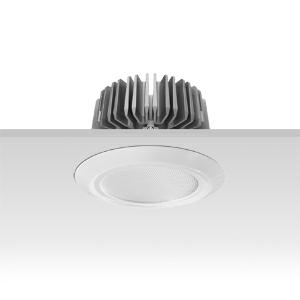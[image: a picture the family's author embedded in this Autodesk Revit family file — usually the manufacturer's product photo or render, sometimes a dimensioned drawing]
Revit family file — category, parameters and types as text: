
# Revit family: 3f_filippi_-_3f_reno_bianco_ampio_3f_filippi_-_30375_a01046_-_3f_reno_150_wh_2000-840_dali_wide___smp_wh_1bde
name_source: partatom
category: Lighting Fixtures
units: mm (PartAtom-declared; Revit-internal decimal feet)

## family parameters
Cut with Voids When Loaded = No
Host = Face
Light Source = No
Part Type = Normal
Room Calculation Point = No
Round Connector Dimension = Use Diameter
Shared = No

## types (1)
- 3F Filippi - 3F Reno Bianco Ampio (1 x LED, 1726 lm, 20 W, 4000 K)
    Apparent Load = 20 VA
    Approval mark = CE
    CIE Flux Codes = 73 92 98 100 100
    Color Rendering = 80
    Color Temperature = 4000 K
    Control Gear = Electronic transformer
    Default Elevation = 1800 mm
    Description = ILLUMINOTECHNICAL
Luminous efficiency 100% (DLOR 100%, ULOR 0%).
Initial luminous flux of the luminaire 1726 lm.
Direct symmetric wide distribution.
Installation Interdistance Transv.D = 1.01 x hu - Long.D = 1.00 x hu.
Tabular UGR (CIE 117 - 4H-8H; S=0.25H; 70/50/20): RUG 23.4 - 23.4.
Beam angle: 70° - 70°.
Luminous efficacy 86 lm/W.
Lifetime (L90/B10): 30000 h. (tq+25°C)
Lifetime (L85/B10): 50000 h. (tq+25°C)
Lifetime (L70/B10): 80000 h. (tq+25°C)
Sudden decreased luminous flux after 50000 hours: 0% (C0).
Photobiological safety in compliance with IEC/TR 62778: RG0 risk exempt, (IEC 62471).
In compliance with IEC/EN 62722-2-1 - IEC/EN 62717 standards.

SOURCE
Compact LED module 2000/840.
Energy efficiency class (UE 2019/2020 - UE 2019/2015): D.
CIE 13.3 Colour rendering index: CRI >80 (R9 <50%).
IES TM-30 Fidelity Index: Rf = 84 Rg = 95.
CCT nominal colour temperature 4000 K.
Colour initial tolerance (MacAdam): SDCM 3.
Zhaga Book 3 compliant.

MECHANICAL
Passive heat dissipator in die-casting aluminium, oversized, for optimum thermal management of the LED module.
Parabolic element with graduated/concentric rings in white polycarbonate.
Transparent external lens with glossy and satin differentiated surfaces, with a cooling and anti-insect system in methacrylate (PMMA).
Fastening spring clips in stainless steel.
Dimensions: diameter 176 mm, height 111 mm. Weight 0.78 kg.
IP44 protection degree for exposed part, IP20 for recessed part.
Mechanical strength to impacts IK05 (0.7 joule).
Glow-wire test resistance 650°C.

ELECTRICAL
Wiring on a separate unit.
Halogen Free DALI-2 DATI (Parts 251, 252, 253), PUSH-DIM, electronic wiring 230V-50/60Hz, power factor 0.90 at full load, THD <25%, constant output current, SELV, class II, 1 driver, 1 DALI addresse.
Power of the luminaire 20 W.
ENEC - CE.
SAFE FLICKER: PstLM=<1 and SVM=<0.4 (IEC TR 61547-1 and IEC TR 63158), to ensure a more comfortable and safe light.
Luminaire compliant with EN 60598-2-22 for power supply from a centralised emergency system CPSS (Central Power Supply System), not incorporated in the luminaire - high risk areas excluded. The default power and flux are 100% in AC and 100% in DC.
Ambient temperature from 0°C to +25°C.
Temperature class T6 max 85°C.
Relative humidity UR: <85%.

INSTALLATION
Pull-up recessed fitting.
False ceiling carving: 150 mm.
All accessories dedicated to this product are available on the Catalog and on our website www.3F-Filippi.com.

ACCESSORIES
A01046 - Anti-glare microprismatic SMP diffuser in methacrylate (PMMA), locked and in line with the trim, in white polycarbonate.

APPLICATIONS
Suitable product for food production plants (HACCP), IFS (Food Version 6), BRC (GSFS Food Version 7).
Environments: architectural, commercial, exhibition areas, transit areas, corridors, shops, display windows, service areas.
In false ceilings with narrow voids.

LIGHT MANAGEMENT
Recommended minimum setting: 10%.
The luminaire, equipped with (DALI-2 DATI) driver, can be controlled manually with 3F Easy Dim technology or automatically/manually with wired or wireless DALI/D2D control systems.
The D2D driver guarantees interoperability with other devices with the same certification by making the following information available:
Device Data (Part 251), Energy Report (Part 252), Diagnosis & Maintenance (Part 253).
In electrical systems without a regulation system (manual or automatic) and DALI bus, a suitable jumper must be made on the DA-DA terminals of the appliance.

WARNING
Luminaire designed for disposal/recycling at end-of-life.
Replaceable (LED only) light source by a professional. Replaceable control gear by a professional.
    Height = 0 mm  [stored 0 ft]
    Lamp = 1 x LED
    Lamp Light Flux = 1726 lm
    Lamp Power = 20 W
    Lamp count = 1
    Length = 176 mm
    Lifetime = 50000 h
    Luminous efficacy = 86 lm/W
    Manufacturer = 3F Filippi
    ModVariant = No
    Model = 3F Filippi - 30375+A01046 - 3F Reno 150 WH 2000-840 DALI WIDE + SMP WH
    Mounting Place = Ceiling
    Mounting Type = Recessed
    Number of Poles = 1
    OnlyDefault = Yes
    Power Factor = 1
    Product Name = 3F Filippi - 3F Reno Bianco Ampio
    Product group = recessed luminaire
    ProductGroupID = 4
    Protection Class = Protection class II
    Protection Degree = IP 20
    RLX_Detail_Level = 1
    RLX_Emergency_Light_Flux = 0 lm
    RLX_Emergency_Type = 0
    RLX_Emergency_Type_DB = No
    RlxData = <blob elided: 85829 chars, md5=a4af8f1c>
    Socket = socket
    Standby Power = 0 W
    System Light Flux = 1726 lm
    System Power = 20 W
    Type Comments = Product without accessories
    Type Image = 3ffilippi_3f_reno_150_wh_vs_smp.jpg
    URL = http://relux.com
    VarID = ---
    Voltage = 0 V
    Weight = 0.00 kg
    Width = 0 mm  [stored 0 ft]

note: [stored X ft] marks values corroborated as IEEE doubles in the binary element streams (Revit-internal decimal feet)

## geometry (parser evidence)
native form markers: Blend x4, Sweep x10
no freeform markers — native parametric forms only
